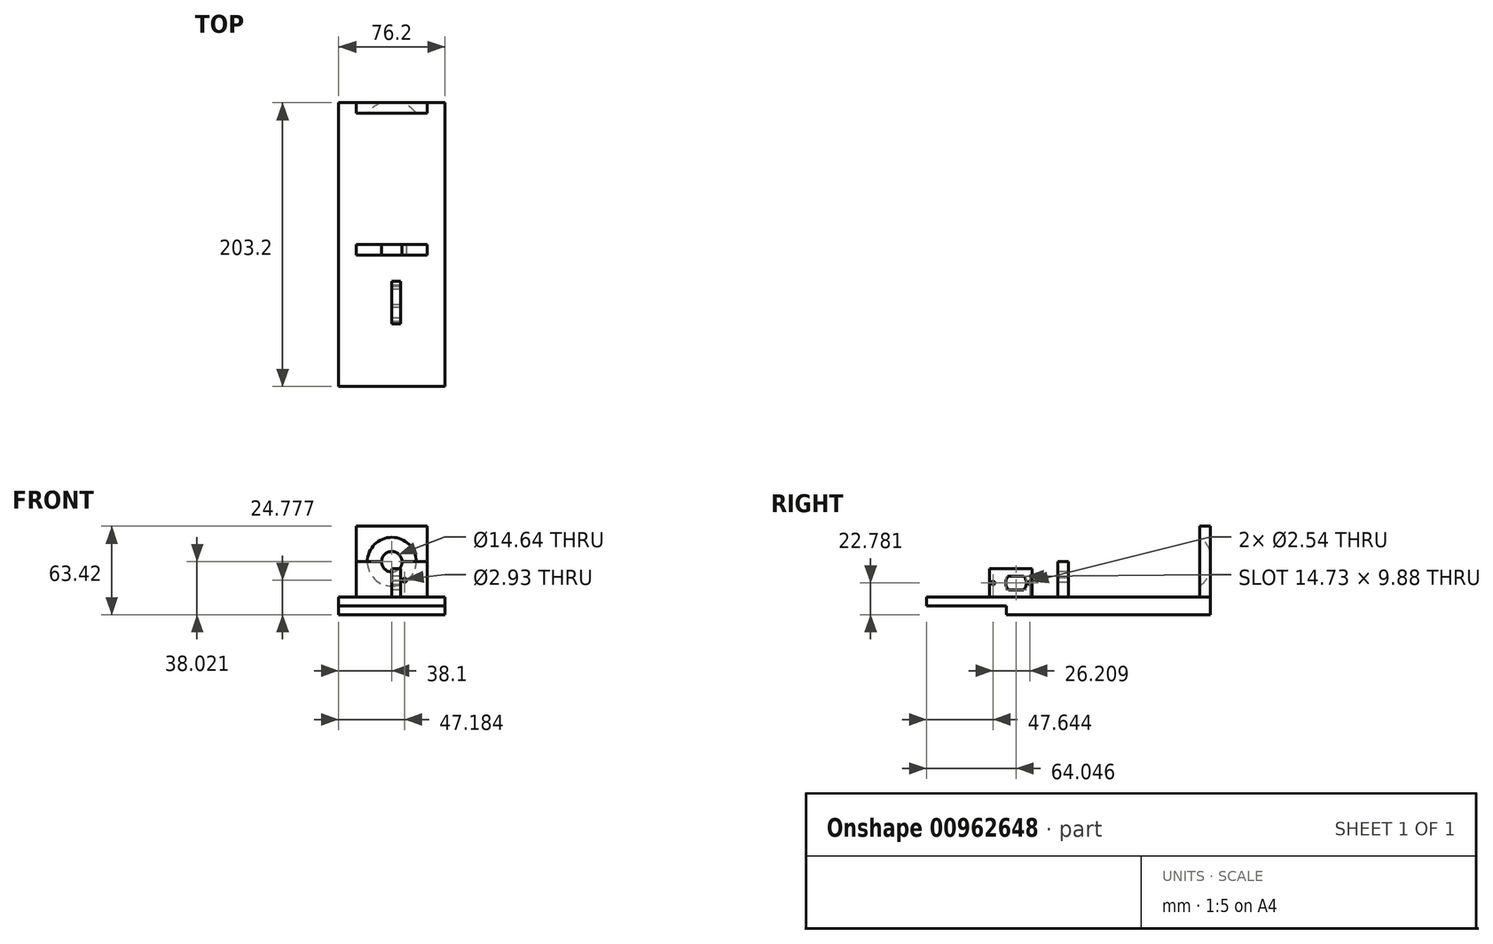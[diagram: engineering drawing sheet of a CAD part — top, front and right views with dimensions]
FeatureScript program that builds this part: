
annotation { "Feature Type Name" : "Feature", "Feature Type Description" : "" }
export const myFeature = defineFeature(function(context is Context, id is Id, definition is map)
    precondition{}
    {
        {
            var Q0;
            Q0=qCreatedBy(makeId("Right.planeOp"),FACE);
            var sketch = newSketch(context, id + "F0", { "sketchPlane" : qUnion([Q0])});
            skLineSegment(sketch, "E0.bottom", {"start": v(-101.6, 6.31) * mm, "end": v(101.6, 6.31) * mm});
            skLineSegment(sketch, "E0.top", {"start": v(-44.45, -6.31) * mm, "end": v(101.6, -6.31) * mm});
            skLineSegment(sketch, "E0.left", {"start": v(-101.6, 6.31) * mm, "end": v(-101.6, 0) * mm});
            skLineSegment(sketch, "E0.right", {"start": v(101.6, 6.31) * mm, "end": v(101.6, -6.31) * mm});
            skPoint(sketch, "E0.middle", {"position": v(0, 0) * mm});
            skLineSegment(sketch, "E1.bottom", {"start": v(101.6, 6.31) * mm, "end": v(93.98, 6.31) * mm});
            skLineSegment(sketch, "E1.top", {"start": v(101.6, 57.11) * mm, "end": v(93.98, 57.11) * mm});
            skLineSegment(sketch, "E1.left", {"start": v(101.6, 6.31) * mm, "end": v(101.6, 57.11) * mm});
            skLineSegment(sketch, "E1.right", {"start": v(93.98, 6.31) * mm, "end": v(93.98, 57.11) * mm});
            skPoint(sketch, "E1.middle", {"position": v(97.79, 31.71) * mm});
            skLineSegment(sketch, "E2.bottom", {"start": v(0, 6.31) * mm, "end": v(-7.62, 6.31) * mm});
            skLineSegment(sketch, "E2.top", {"start": v(0, 31.71) * mm, "end": v(-7.62, 31.71) * mm});
            skLineSegment(sketch, "E2.left", {"start": v(0, 6.31) * mm, "end": v(0, 31.71) * mm});
            skLineSegment(sketch, "E2.right", {"start": v(-7.62, 6.31) * mm, "end": v(-7.62, 31.71) * mm});
            skPoint(sketch, "E2.middle", {"position": v(-3.81, 19.01) * mm});
            skLineSegment(sketch, "E3.top", {"start": v(-26.12, 26.63) * mm, "end": v(-56.6, 26.63) * mm});
            skLineSegment(sketch, "E3.left", {"start": v(-26.12, 6.31) * mm, "end": v(-26.12, 26.63) * mm});
            skLineSegment(sketch, "E3.right", {"start": v(-56.6, 6.31) * mm, "end": v(-56.6, 26.63) * mm});
            skArc(sketch, "E4", {"start": v(-32.09, 11.53) * mm, "mid": v(-30.19, 16.47) * mm, "end": v(-32.09, 21.41) * mm});
            skPoint(sketch, "E5.oppositeSnap0", {"position": v(-101.6, 0) * mm});
            skLineSegment(sketch, "E5.top", {"start": v(-101.6, 0) * mm, "end": v(-44.45, 0) * mm});
            skLineSegment(sketch, "E5.right", {"start": v(-44.45, -6.31) * mm, "end": v(-44.45, 0) * mm});
            skPoint(sketch, "E6.orphan", {"position": v(-101.6, -6.31) * mm});
            skLineSegment(sketch, "E7", {"start": v(-26.12, 16.47) * mm, "end": v(-56.6, 16.47) * mm, "construction": true});
            skCircle(sketch, "E8", {"center": v(-53.96, 16.47) * mm, "radius": 1.27 * mm});
            skCircle(sketch, "E9", {"center": v(-27.75, 16.47) * mm, "radius": 1.27 * mm});
            skLineSegment(sketch, "E10.bottom", {"start": v(-32.09, 21.41) * mm, "end": v(-43.02, 21.41) * mm});
            skLineSegment(sketch, "E10.top", {"start": v(-32.09, 11.53) * mm, "end": v(-43.02, 11.53) * mm});
            skArc(sketch, "E11.trimOffspring", {"start": v(-43.02, 21.41) * mm, "mid": v(-44.92, 16.47) * mm, "end": v(-43.02, 11.53) * mm});
            skSolve(sketch);
        }
        {
            var Q0;
            Q0=makeQuery(id+"F0.imprint","IMPRINT",FACE,{"disambiguationData":[TD([[makeQuery(id+"F0.imprint","IMPRINT",EDGE,{"derivedFrom":sQuery(id+"F0.wireOp",EDGE,"E0.top")}),1.0]])]});
            extrude(context, id + "F1", {"entities" : qUnion([Q0]), "endBound" : BoundingType.SYMMETRIC, "depth" : 76.2 * mm, "offsetDistance" : 25.4 * mm});
        }
        {
            var Q0;
            Q0=makeQuery(id+"F0.imprint","IMPRINT",FACE,{"disambiguationData":[TD([[makeQuery(id+"F0.imprint","IMPRINT",EDGE,{"derivedFrom":sQuery(id+"F0.wireOp",EDGE,"E3.top")}),1.0]])]});
            extrude(context, id + "F2", {"entities" : qUnion([Q0]), "operationType" : NewBodyOperationType.ADD, "depth" : 6.35 * mm, "offsetDistance" : 25.4 * mm});
        }
        {
            var Q0;
            Q0=makeQuery(id+"F0.imprint","IMPRINT",FACE,{"disambiguationData":[TD([[makeQuery(id+"F0.imprint","IMPRINT",EDGE,{"derivedFrom":sQuery(id+"F0.wireOp",EDGE,"E2.top")}),1.0]])]});
            extrude(context, id + "F3", {"entities" : qUnion([Q0]), "operationType" : NewBodyOperationType.ADD, "endBound" : BoundingType.SYMMETRIC, "depth" : 50.8 * mm, "offsetDistance" : 25.4 * mm});
        }
        {
            var Q0;
            Q0=makeQuery(id+"F0.imprint","IMPRINT",FACE,{"disambiguationData":[TD([[makeQuery(id+"F0.imprint","IMPRINT",EDGE,{"derivedFrom":sQuery(id+"F0.wireOp",EDGE,"E1.top")}),1.0]])]});
            extrude(context, id + "F4", {"entities" : qUnion([Q0]), "operationType" : NewBodyOperationType.ADD, "endBound" : BoundingType.SYMMETRIC, "depth" : 50.8 * mm, "offsetDistance" : 25.4 * mm});
        }
        {
            var Q0;
            Q0=qCreatedBy(makeId("Right.planeOp"),FACE);
            var sketch = newSketch(context, id + "F5", { "sketchPlane" : qUnion([Q0])});
            skArc(sketch, "E12", {"start": v(81.28, 53.3) * mm, "mid": v(59.69, 31.71) * mm, "end": v(81.28, 10.12) * mm});
            skLineSegment(sketch, "E13", {"start": v(81.28, 53.3) * mm, "end": v(81.28, 10.12) * mm});
            skSolve(sketch);
        }
        {
            var Q0;
            Q0=makeQuery(id+"F5.imprint","IMPRINT",FACE,{"disambiguationData":[TD([[makeQuery(id+"F5.imprint","IMPRINT",EDGE,{"derivedFrom":sQuery(id+"F5.wireOp",EDGE,"E12")}),1.0]])]});
            var Q1;
            Q1=sQuery(id+"F5.wireOp",EDGE,"E13");
            revolve(context, id + "F6", {"operationType" : NewBodyOperationType.REMOVE, "surfaceOperationType" : NewSurfaceOperationType.NEW, "entities" : qUnion([Q0]), "axis" : qUnion([Q1]), "revolveType" : RevolveType.FULL, "oppositeDirection" : true});
        }
        {
            var Q0;
            Q0=makeQuery(id+"F3.opExtrude","SWEPT_FACE",FACE,{"disambiguationData":[OSD([sQuery(id+"F0.wireOp",EDGE,"E2.right")])]});
            var sketch = newSketch(context, id + "F7", { "sketchPlane" : qUnion([Q0])});
            skCircle(sketch, "E14", {"center": v(0, 31.71) * mm, "radius": 7.32 * mm});
            skSolve(sketch);
        }
        {
            var Q0;
            Q0 = qSketchRegion(id + "F7", true);
            extrude(context, id + "F8", {"entities" : qUnion([Q0]), "operationType" : NewBodyOperationType.REMOVE, "endBound" : BoundingType.THROUGH_ALL, "oppositeDirection" : true, "depth" : 25.4 * mm, "offsetDistance" : 25.4 * mm});
        }
        {
            var Q0;
            Q0=makeQuery(id+"F3.opExtrude","SWEPT_FACE",FACE,{"disambiguationData":[OSD([sQuery(id+"F0.wireOp",EDGE,"E2.right")])]});
            var sketch = newSketch(context, id + "F9", { "sketchPlane" : qUnion([Q0])});
            skCircle(sketch, "E15", {"center": v(9.08, 18.47) * mm, "radius": 1.46 * mm});
            skSolve(sketch);
        }
        {
            var Q0;
            Q0=makeQuery(id+"F9.imprint","IMPRINT",FACE,{"disambiguationData":[TD([[makeQuery(id+"F9.imprint","IMPRINT",EDGE,{"derivedFrom":sQuery(id+"F9.wireOp",EDGE,"E15")}),1.0]])]});
            extrude(context, id + "F10", {"entities" : qUnion([Q0]), "operationType" : NewBodyOperationType.REMOVE, "oppositeDirection" : true, "depth" : 25.4 * mm, "offsetDistance" : 25.4 * mm});
        }
    });
